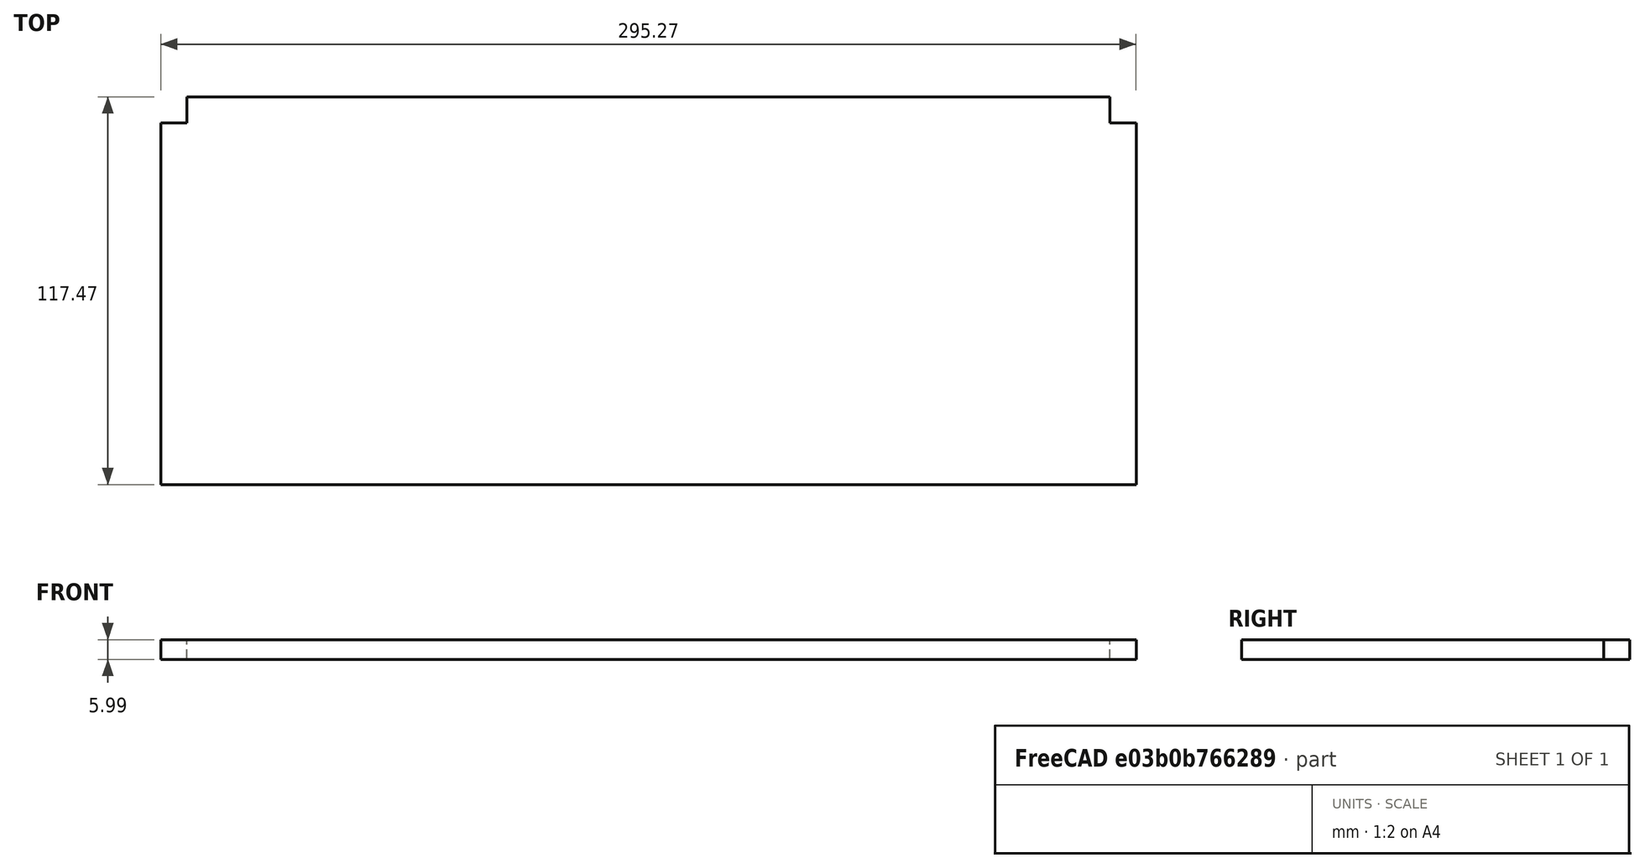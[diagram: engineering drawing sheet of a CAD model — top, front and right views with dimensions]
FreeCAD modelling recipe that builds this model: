
FCSTD DOCUMENT  (FreeCAD 0.19R24267 (Git))
Label: Inv2-P12
License: All rights reserved
LicenseURL: http://en.wikipedia.org/wiki/All_rights_reserved
objects: TechDraw::DrawViewDimension×7, TechDraw::DrawProjGroupItem×2, TechDraw::DrawHatch×2, TechDraw::DrawViewAnnotation×2, Sketcher::SketchObject×1, Part::Extrusion×1, TechDraw::DrawSVGTemplate×1, TechDraw::DrawProjGroup×1, TechDraw::DrawPage×1
note: 2 computed .brp shape members not serialized (recipe doc carries the construction recipe); baked Part::Feature solids carry a one-line shape summary decoded from their .brp

FEATURE [Sketcher::SketchObject] Sketch
  FullyConstrained = true
  sketch-geometry (8):
    g0: LineSegment StartX=0 StartY=0 StartZ=0 EndX=295.275 EndY=0 EndZ=0
    g1: LineSegment StartX=0 StartY=0 StartZ=0 EndX=0 EndY=109.525 EndZ=0
    g2: LineSegment StartX=0 StartY=109.525 StartZ=0 EndX=7.9502 EndY=109.525 EndZ=0
    g3: LineSegment StartX=7.9502 StartY=117.475 StartZ=0 EndX=287.325 EndY=117.475 EndZ=0
    g4: LineSegment StartX=287.325 StartY=117.475 StartZ=0 EndX=287.325 EndY=109.525 EndZ=0
    g5: LineSegment StartX=287.325 StartY=109.525 StartZ=0 EndX=295.275 EndY=109.525 EndZ=0
    g6: LineSegment StartX=295.275 StartY=109.525 StartZ=0 EndX=295.275 EndY=0 EndZ=0
    g7: LineSegment StartX=7.9502 StartY=109.525 StartZ=0 EndX=7.9502 EndY=117.475 EndZ=0
  constraints (23):
    c: Coincident(g0,g-1)
    c: PointOnObject(g0,g-1)
    c: Coincident(g1,g0)
    c: PointOnObject(g1,g-2)
    c: Coincident(g2,g1)
    c: Horizontal(g2)
    c: Horizontal(g3)
    c: Coincident(g4,g3)
    c: Coincident(g6,g5)
    c: Coincident(g6,g0)
    c: Vertical(g6)
    c: Horizontal(g5)
    c: Vertical(g4)
    c: DistanceX(g0,g0) = 295.275
    c: Distance(g3,g0) = 117.475
    c: DistanceX(g2,g2) = 7.9502
    c: Equal(g5,g2)
    c: Coincident(g5,g4)
    c: Equal(g4,g2)
    c: Coincident(g7,g2)
    c: Coincident(g7,g3)
    c: Vertical(g7)
    c: Equal(g7,g2)
FEATURE [Part::Extrusion] Extrude
  Base = -> Sketch
  Dir = (0,0,1)
  DirMode = 2
  FaceMakerClass = Part::FaceMakerBullseye
  LengthFwd = 5.9944
  LengthRev = 0
  Solid = true
  Symmetric = false
FEATURE [TechDraw::DrawSVGTemplate] Template
  Height = 215.9
  Orientation = 1
  Width = 279.4
FEATURE [TechDraw::DrawProjGroupItem] ProjItem  label="Front"
  CoarseView = false
  Direction = (0,0,1)
  Focus = 100
  HardHidden = false
  IsoCount = 0
  IsoHidden = false
  IsoVisible = false
  LockPosition = true
  Perspective = false
  Rotation = 0
  RotationVector = (1,0,0)
  Scale = 0.5
  ScaleType = 2
  SeamHidden = false
  SeamVisible = true
  SmoothHidden = false
  SmoothVisible = true
  Source = -> [Extrude]
  Type = 0
  X = 0
  XDirection = (1,0,0)
  Y = 0
FEATURE [TechDraw::DrawProjGroupItem] ProjItem001  label="Left"
  CoarseView = false
  Direction = (-1,0,1e-16)
  Focus = 100
  HardHidden = false
  IsoCount = 0
  IsoHidden = false
  IsoVisible = false
  LockPosition = false
  Perspective = false
  Rotation = 0
  RotationVector = (1,0,0)
  ScaleType = 2
  SeamHidden = false
  SeamVisible = true
  SmoothHidden = false
  SmoothVisible = true
  Source = -> [Extrude]
  Type = 1
  X = 120.141
  XDirection = (1e-16,0,1)
  Y = 0
FEATURE [TechDraw::DrawProjGroup] ProjGroup
  Anchor = -> ProjItem
  AutoDistribute = true
  LockPosition = false
  ProjectionType = 0
  Rotation = 0
  Scale = 0.5
  ScaleType = 2
  Source = -> [Extrude]
  Views = -> [ProjItem,ProjItem001]
  X = 117.656
  Y = 108.257
  spacingX = 15.0114
  spacingY = 15.0114
FEATURE [TechDraw::DrawViewDimension] Dimension
  Arbitrary = false
  ArbitraryTolerances = false
  EqualTolerance = true
  FormatSpec = %.3f
  FormatSpecOverTolerance = %+.3f
  FormatSpecUnderTolerance = %+.3f
  Inverted = false
  LockPosition = false
  MeasureType = 1
  OverTolerance = 0
  References2D = -> [ProjItem]
  Rotation = 0
  ScaleType = 0
  TheoreticalExact = false
  Type = 1
  UnderTolerance = 0
  X = -1.47372
  Y = -44.106
FEATURE [TechDraw::DrawViewDimension] Dimension001
  Arbitrary = false
  ArbitraryTolerances = false
  EqualTolerance = true
  FormatSpec = %.3f
  FormatSpecOverTolerance = %+.3f
  FormatSpecUnderTolerance = %+.3f
  Inverted = false
  LockPosition = false
  MeasureType = 1
  OverTolerance = 0
  References2D = -> [ProjItem001]
  Rotation = 0
  ScaleType = 0
  TheoreticalExact = false
  Type = 1
  UnderTolerance = 0
  X = 14.072
  Y = 14.7851
FEATURE [TechDraw::DrawViewDimension] Dimension002
  Arbitrary = false
  ArbitraryTolerances = false
  EqualTolerance = true
  FormatSpec = %.3f
  FormatSpecOverTolerance = %+.3f
  FormatSpecUnderTolerance = %+.3f
  Inverted = false
  LockPosition = false
  MeasureType = 1
  OverTolerance = 0
  References2D = -> [ProjItem]
  Rotation = 0
  ScaleType = 0
  TheoreticalExact = false
  Type = 2
  UnderTolerance = 0
  X = 97.0154
  Y = 1.12576
FEATURE [TechDraw::DrawViewDimension] Dimension003
  Arbitrary = false
  ArbitraryTolerances = false
  EqualTolerance = true
  FormatSpec = %.3f
  FormatSpecOverTolerance = %+.3f
  FormatSpecUnderTolerance = %+.3f
  Inverted = false
  LockPosition = false
  MeasureType = 1
  OverTolerance = 0
  References2D = -> [ProjItem]
  Rotation = 0
  ScaleType = 0
  TheoreticalExact = false
  Type = 1
  UnderTolerance = 0
  X = 86.8072
  Y = 19.0399
FEATURE [TechDraw::DrawViewDimension] Dimension004
  Arbitrary = false
  ArbitraryTolerances = false
  EqualTolerance = true
  FormatSpec = %.3f
  FormatSpecOverTolerance = %+.3f
  FormatSpecUnderTolerance = %+.3f
  Inverted = false
  LockPosition = false
  MeasureType = 1
  OverTolerance = 0
  References2D = -> [ProjItem]
  Rotation = 0
  ScaleType = 0
  TheoreticalExact = false
  Type = 2
  UnderTolerance = 0
  X = 54.7434
  Y = 47.6311
FEATURE [TechDraw::DrawViewDimension] Dimension005
  Arbitrary = false
  ArbitraryTolerances = false
  EqualTolerance = true
  FormatSpec = %.3f
  FormatSpecOverTolerance = %+.3f
  FormatSpecUnderTolerance = %+.3f
  Inverted = false
  LockPosition = false
  MeasureType = 1
  OverTolerance = 0
  References2D = -> [ProjItem]
  Rotation = 0
  ScaleType = 0
  TheoreticalExact = false
  Type = 2
  UnderTolerance = 0
  X = -62.4751
  Y = 45.1887
FEATURE [TechDraw::DrawViewDimension] Dimension006
  Arbitrary = false
  ArbitraryTolerances = false
  EqualTolerance = true
  FormatSpec = %.3f
  FormatSpecOverTolerance = %+.3f
  FormatSpecUnderTolerance = %+.3f
  Inverted = false
  LockPosition = false
  MeasureType = 1
  OverTolerance = 0
  References2D = -> [ProjItem]
  Rotation = 0
  ScaleType = 0
  TheoreticalExact = false
  Type = 1
  UnderTolerance = 0
  X = -91.7878
  Y = 18.3321
FEATURE [TechDraw::DrawHatch] Hatch  label="HatchF0"
  HatchPattern = <path>
  Source = -> ProjItem [Face0]
FEATURE [TechDraw::DrawHatch] Hatch001  label="Hatch001F1"
  HatchPattern = <path>
  Source = -> ProjItem001 [Face1,Face2]
FEATURE [TechDraw::DrawViewAnnotation] Annotation
  Font = osifont
  LineSpace = 80
  LockPosition = false
  MaxWidth = -1
  Rotation = 0
  ScaleType = 0
  Text = Figure S2 (Inverted 2) | Panel 12 [camera top] | Quantity: 1
  TextSize = 5.0038
  TextStyle = 0
  X = 32.8152
  Y = 195.58
FEATURE [TechDraw::DrawViewAnnotation] Annotation002
  Font = osifont
  LineSpace = 80
  LockPosition = false
  MaxWidth = -1
  Rotation = 0
  ScaleType = 0
  Text = Units: Inches
  TextSize = 5.0038
  TextStyle = 0
  X = 259.08
  Y = 5.08
FEATURE [TechDraw::DrawPage] Page
  KeepUpdated = true
  NextBalloonIndex = 1
  ProjectionType = 0
  Template = -> Template
  Views = -> [ProjGroup,Dimension,Dimension001,Dimension002,Dimension003,Dimension004,Dimension005,Dimension006,Annotation,Annotation002]
note: 2 file-system paths scrubbed to <path> (originals preserved in the JSON sidecar)
